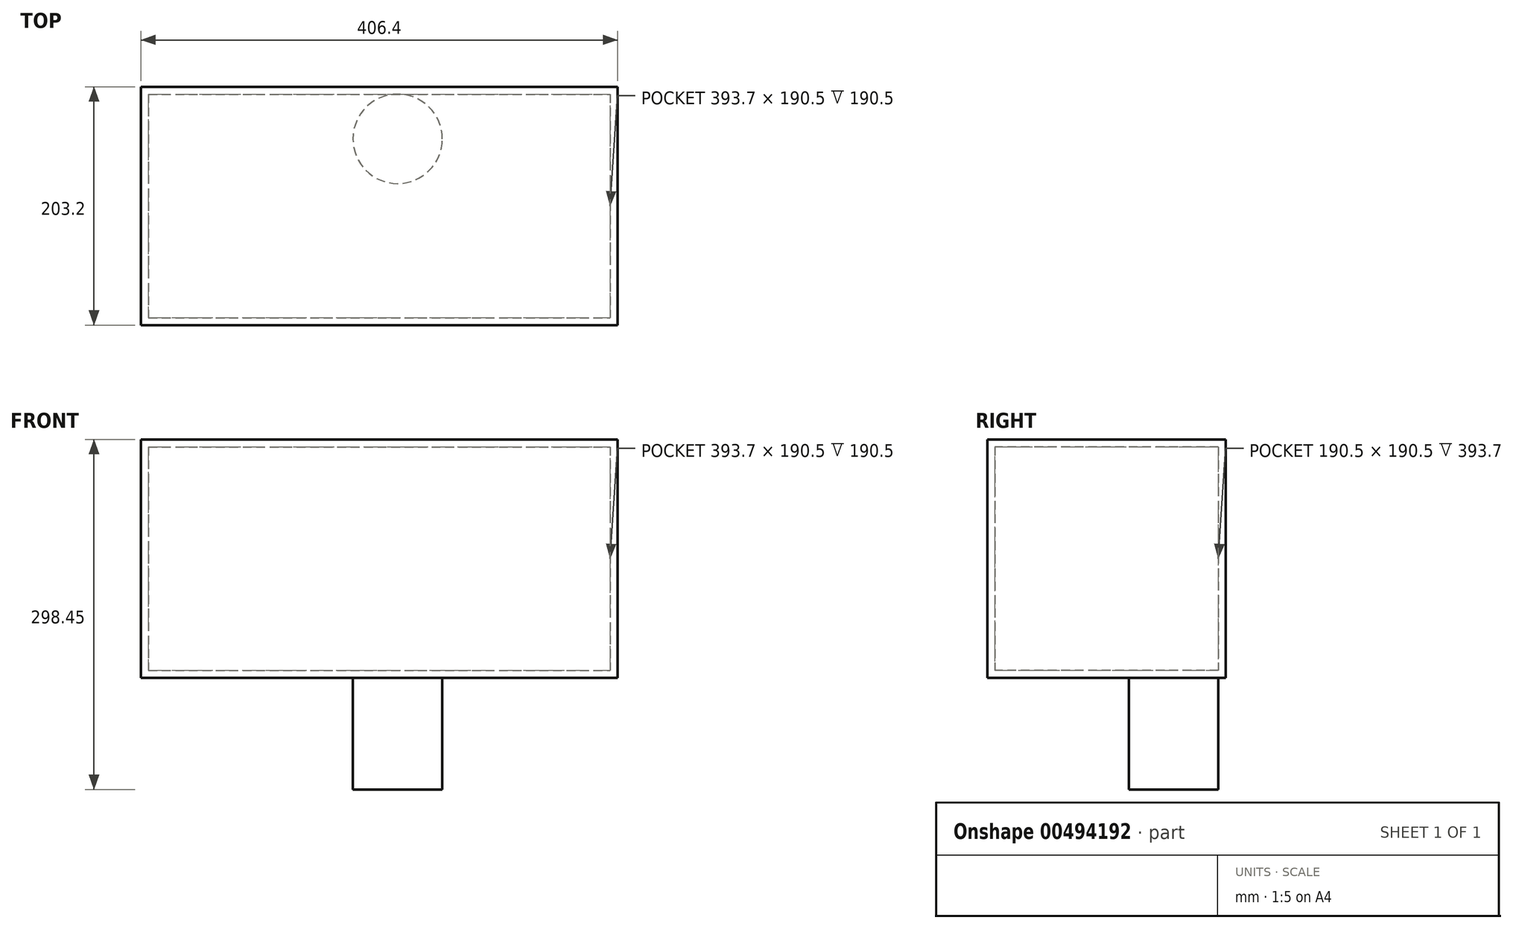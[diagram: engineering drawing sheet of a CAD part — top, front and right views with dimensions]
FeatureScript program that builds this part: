
annotation { "Feature Type Name" : "Feature", "Feature Type Description" : "" }
export const myFeature = defineFeature(function(context is Context, id is Id, definition is map)
    precondition{}
    {
        {
            var Q0;
            Q0=qCreatedBy(makeId("Top.planeOp"),FACE);
            var sketch = newSketch(context, id + "F0", { "sketchPlane" : qUnion([Q0])});
            skLineSegment(sketch, "E0.bottom", {"start": v(-204.87, 39.09) * mm, "end": v(201.53, 39.09) * mm});
            skLineSegment(sketch, "E0.top", {"start": v(-204.87, -164.11) * mm, "end": v(201.53, -164.11) * mm});
            skLineSegment(sketch, "E0.left", {"start": v(-204.87, 39.09) * mm, "end": v(-204.87, -164.11) * mm});
            skLineSegment(sketch, "E0.right", {"start": v(201.53, 39.09) * mm, "end": v(201.53, -164.11) * mm});
            skSolve(sketch);
        }
        {
            var Q0;
            Q0 = qSketchRegion(id + "F0", true);
            extrude(context, id + "F1", {"entities" : qUnion([Q0]), "endBound" : BoundingType.SYMMETRIC, "depth" : 203.2 * mm});
        }
        {
            var Q0;
            Q0=makeQuery(id+"F1.opExtrude","SWEPT_FACE",FACE,{"disambiguationData":[OSD([sQuery(id+"F0.wireOp",EDGE,"E0.top")])]});
            var sketch = newSketch(context, id + "F2", { "sketchPlane" : qUnion([Q0])});
            skLineSegment(sketch, "E1.bottom", {"start": v(-198.52, 95.25) * mm, "end": v(195.18, 95.25) * mm});
            skLineSegment(sketch, "E1.top", {"start": v(-198.52, -95.25) * mm, "end": v(195.18, -95.25) * mm});
            skLineSegment(sketch, "E1.left", {"start": v(-198.52, 95.25) * mm, "end": v(-198.52, -95.25) * mm});
            skLineSegment(sketch, "E1.right", {"start": v(195.18, 95.25) * mm, "end": v(195.18, -95.25) * mm});
            skSolve(sketch);
        }
        {
            var Q0;
            Q0=makeQuery(id+"F2.imprint","IMPRINT",FACE,{"disambiguationData":[TD([[makeQuery(id+"F2.imprint","IMPRINT",EDGE,{"derivedFrom":sQuery(id+"F2.wireOp",EDGE,"E1.bottom")}),-1.0]])]});
            cPlane(context, id + "F3", {"entities" : qUnion([Q0]), "cplaneType" : CPlaneType.OFFSET, "offset" : 6.35 * mm, "oppositeDirection" : true, "width" : 152.4 * mm, "height" : 152.4 * mm});
        }
        {
            var Q0;
            Q0=qCreatedBy(id+"F3.planeOp",FACE);
            var sketch = newSketch(context, id + "F4", { "sketchPlane" : qUnion([Q0])});
            skLineSegment(sketch, "E2.bottom", {"start": v(-198.52, 95.25) * mm, "end": v(195.18, 95.25) * mm});
            skLineSegment(sketch, "E2.top", {"start": v(-198.52, -95.25) * mm, "end": v(195.18, -95.25) * mm});
            skLineSegment(sketch, "E2.left", {"start": v(-198.52, 95.25) * mm, "end": v(-198.52, -95.25) * mm});
            skLineSegment(sketch, "E2.right", {"start": v(195.18, 95.25) * mm, "end": v(195.18, -95.25) * mm});
            skSolve(sketch);
        }
        {
            var Q0;
            Q0 = qSketchRegion(id + "F4", true);
            extrude(context, id + "F5", {"entities" : qUnion([Q0]), "operationType" : NewBodyOperationType.REMOVE, "oppositeDirection" : true, "depth" : 190.5 * mm});
        }
        {
            var Q0;
            Q0=makeQuery(id+"F1.opExtrude","CAP_FACE",FACE,{"disambiguationData":[OSD([sQuery(id+"F0.wireOp",EDGE,"E0.bottom"),sQuery(id+"F0.wireOp",EDGE,"E0.top"),sQuery(id+"F0.wireOp",EDGE,"E0.left"),sQuery(id+"F0.wireOp",EDGE,"E0.right")])],"isStart":true});
            var sketch = newSketch(context, id + "F6", { "sketchPlane" : qUnion([Q0])});
            skCircle(sketch, "E3", {"center": v(13.96, 5.36) * mm, "radius": 38.1 * mm});
            skSolve(sketch);
        }
        {
            var Q0;
            Q0 = qSketchRegion(id + "F6", true);
            extrude(context, id + "F7", {"entities" : qUnion([Q0]), "operationType" : NewBodyOperationType.REMOVE, "endBound" : BoundingType.UP_TO_NEXT, "oppositeDirection" : true, "depth" : 25.4 * mm});
        }
        {
            var Q0;
            Q0=makeQuery(id+"F1.opExtrude","CAP_FACE",FACE,{"disambiguationData":[OSD([sQuery(id+"F0.wireOp",EDGE,"E0.bottom"),sQuery(id+"F0.wireOp",EDGE,"E0.top"),sQuery(id+"F0.wireOp",EDGE,"E0.left"),sQuery(id+"F0.wireOp",EDGE,"E0.right")])],"isStart":true});
            cPlane(context, id + "F8", {"entities" : qUnion([Q0]), "cplaneType" : CPlaneType.OFFSET, "offset" : 6.35 * mm, "oppositeDirection" : true, "width" : 152.4 * mm, "height" : 152.4 * mm});
        }
        {
            var Q0;
            Q0=qCreatedBy(id+"F8.planeOp",FACE);
            var sketch = newSketch(context, id + "F9", { "sketchPlane" : qUnion([Q0])});
            skCircle(sketch, "E4", {"center": v(13.96, 5.36) * mm, "radius": 38.1 * mm});
            skLineSegment(sketch, "E5.bottom", {"start": v(-49.54, 68.86) * mm, "end": v(77.46, 68.86) * mm});
            skLineSegment(sketch, "E5.top", {"start": v(-49.54, -32.74) * mm, "end": v(77.46, -32.74) * mm});
            skLineSegment(sketch, "E5.left", {"start": v(-49.54, 68.86) * mm, "end": v(-49.54, -32.74) * mm});
            skLineSegment(sketch, "E5.right", {"start": v(77.46, 68.86) * mm, "end": v(77.46, -32.74) * mm});
            skSolve(sketch);
        }
        {
            var Q0;
            Q0=makeQuery(id+"F9.imprint","IMPRINT",FACE,{"disambiguationData":[TD([[makeQuery(id+"F9.imprint","IMPRINT",EDGE,{"derivedFrom":sQuery(id+"F9.wireOp",EDGE,"E4")}),1.0]])]});
            extrude(context, id + "F10", {"entities" : qUnion([Q0]), "operationType" : NewBodyOperationType.ADD, "depth" : 101.6 * mm});
        }
        {
            var Q0;
            Q0=sQuery(id+"F9.wireOp",EDGE,"E5.left");
            var Q1;
            Q1=sQuery(id+"F9.wireOp",EDGE,"E5.bottom");
            var Q2;
            Q2=sQuery(id+"F9.wireOp",EDGE,"E5.right");
            var Q3;
            Q3=sQuery(id+"F9.wireOp",EDGE,"E5.top");
            extrude(context, id + "F11", {"bodyType" : ToolBodyType.SURFACE, "surfaceEntities" : qUnion([Q0, Q1, Q2, Q3]), "oppositeDirection" : true, "depth" : 12.7 * mm});
        }
    });
